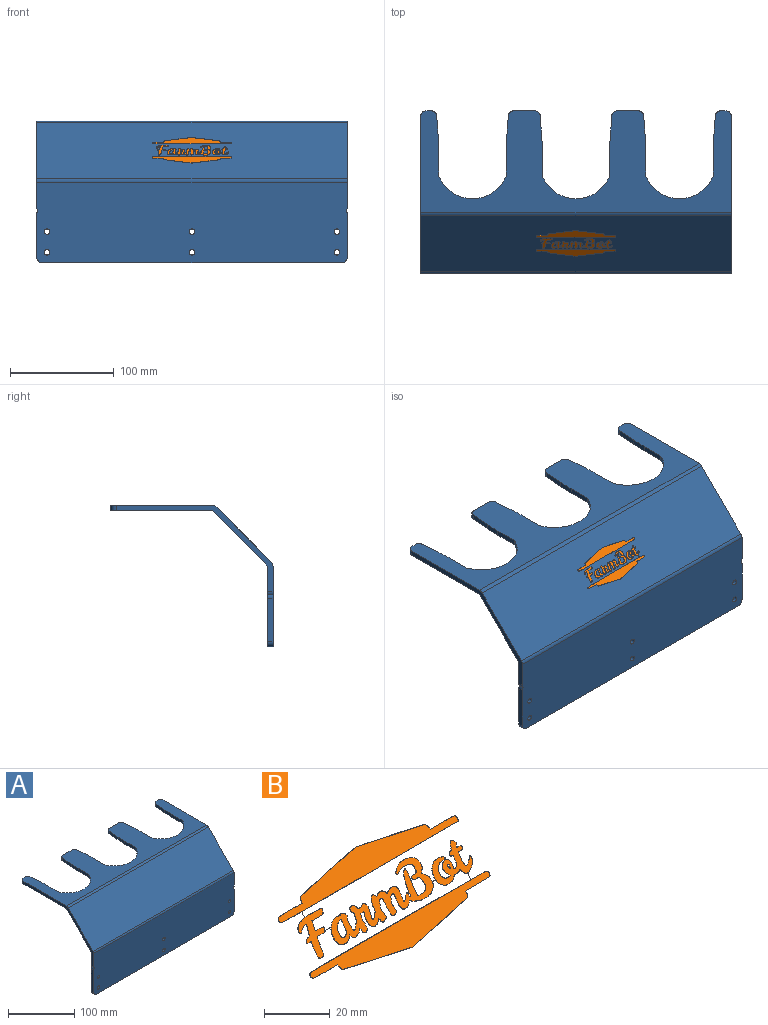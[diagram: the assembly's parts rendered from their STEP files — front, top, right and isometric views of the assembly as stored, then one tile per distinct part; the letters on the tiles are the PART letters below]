
ASSEMBLY  parts=2 mates=1
PART A: 58 faces, bbox 300x156.6x136.6 mm
  f0: plane 300x77.93mm, normal (0,-1,0), area 23234.2mm2, adj f1,f2,f10,f11,f41,f42,f43,f44
  f1: plane 151.57x83.57mm, normal (-1,0,0), area 988.2mm2, adj f0,f3,f4,f6,f39,f40,f42,f45
  f2: plane 151.57x83.57mm, normal (1,0,0), area 988.2mm2, adj f0,f3,f4,f6,f39,f40,f42,f46
  f3: plane 300x77.93mm, normal (0,1,0), area 23234.2mm2, adj f1,f2,f10,f11,f39,f41,f43,f44
  f4: plane 300x97.93mm, normal (0,0,-1), area 13697.5mm2, adj f1,f2,f5,f7,f8,f9,f12,f13
  f5: plane 5.36x5mm, normal (0,1,0), area 26.8mm2, adj f4,f6,f37,f46
  f6: plane 300x97.93mm, normal (0,0,1), area 13697.5mm2, adj f1,f2,f5,f7,f8,f9,f12,f13
  f7: plane 20.73x5mm, normal (0,1,0), area 103.6mm2, adj f4,f6,f28,f38
  f8: plane 20.73x5mm, normal (0,1,0), area 103.6mm2, adj f4,f6,f19,f29
  f9: plane 5.36x5mm, normal (0,1,0), area 26.8mm2, adj f4,f6,f20,f45
  f10: plane 42x5mm, normal (-1,0,0), area 210mm2, adj f0,f3,f43,f55
  f11: plane 42x5mm, normal (1,0,0), area 210mm2, adj f0,f3,f44,f56
  f12: plane 20.82x5mm, normal (-1,0.08,0), area 104.4mm2, adj f4,f6,f18,f19
  f13: plane 20.82x5mm, normal (1,0.08,0), area 104.4mm2, adj f4,f6,f17,f20
  f14: plane 22.43x5mm, normal (1,0,0), area 112.2mm2, adj f4,f6,f15,f17
  f15: cylinder r=35mm len=65mm, axis (0,0,1), area 416.7mm2, adj f4,f6,f14,f16
  f16: plane 22.43x5mm, normal (-1,0,0), area 112.2mm2, adj f4,f6,f15,f18
  f17: cylinder r=200mm len=15.11mm, axis (0,0,1), area 75.6mm2, adj f4,f6,f13,f14
  f18: cylinder r=200mm len=15.11mm, axis (0,0,1), area 75.6mm2, adj f4,f6,f12,f16
  f19: cylinder r=5mm len=5mm, axis (0,0,1), area 37.4mm2, adj f4,f6,f8,f12
  f20: cylinder r=5mm len=5mm, axis (0,0,-1), area 37.4mm2, adj f4,f6,f9,f13
  f21: plane 20.82x5mm, normal (-1,0.08,0), area 104.4mm2, adj f4,f6,f27,f28
  f22: plane 20.82x5mm, normal (1,0.08,0), area 104.4mm2, adj f4,f6,f26,f29
  f23: plane 22.43x5mm, normal (1,0,0), area 112.2mm2, adj f4,f6,f24,f26
  f24: cylinder r=35mm len=65mm, axis (0,0,1), area 416.7mm2, adj f4,f6,f23,f25
  f25: plane 22.43x5mm, normal (-1,0,0), area 112.2mm2, adj f4,f6,f24,f27
  f26: cylinder r=200mm len=15.11mm, axis (0,0,1), area 75.6mm2, adj f4,f6,f22,f23
  f27: cylinder r=200mm len=15.11mm, axis (0,0,1), area 75.6mm2, adj f4,f6,f21,f25
  f28: cylinder r=5mm len=5mm, axis (0,0,1), area 37.4mm2, adj f4,f6,f7,f21
  f29: cylinder r=5mm len=5mm, axis (0,0,-1), area 37.4mm2, adj f4,f6,f8,f22
  f30: plane 20.82x5mm, normal (-1,0.08,0), area 104.4mm2, adj f4,f6,f36,f37
  f31: plane 20.82x5mm, normal (1,0.08,0), area 104.4mm2, adj f4,f6,f35,f38
  f32: plane 22.43x5mm, normal (1,0,0), area 112.2mm2, adj f4,f6,f33,f35
  f33: cylinder r=35mm len=65mm, axis (0,0,1), area 416.7mm2, adj f4,f6,f32,f34
  f34: plane 22.43x5mm, normal (-1,0,0), area 112.2mm2, adj f4,f6,f33,f36
  f35: cylinder r=200mm len=15.11mm, axis (0,0,1), area 75.6mm2, adj f4,f6,f31,f32
  f36: cylinder r=200mm len=15.11mm, axis (0,0,1), area 75.6mm2, adj f4,f6,f30,f34
  f37: cylinder r=5mm len=5mm, axis (0,0,1), area 37.4mm2, adj f4,f5,f6,f30
  f38: cylinder r=5mm len=5mm, axis (0,0,-1), area 37.4mm2, adj f4,f6,f7,f31
  f39: plane 300x53.64mm, normal (0,0.71,-0.71), area 22757.4mm2, adj f1,f2,f3,f4
  f40: plane 300x53.64mm, normal (0,-0.71,0.71), area 22757.4mm2, adj f1,f2,f42,f47
  f41: plane 290x5mm, normal (0,0,-1), area 1450mm2, adj f0,f3,f43,f44
  f42: cylinder r=5mm len=300mm, axis (1,0,0), area 1178.1mm2, adj f0,f1,f2,f40
  f43: cylinder r=5mm len=5mm, axis (0,1,0), area 39.3mm2, adj f0,f3,f10,f41
  f44: cylinder r=5mm len=5mm, axis (0,-1,0), area 39.3mm2, adj f0,f3,f11,f41
  f45: cylinder r=5mm len=5mm, axis (0,0,-1), area 39.3mm2, adj f1,f4,f6,f9
  f46: cylinder r=5mm len=5mm, axis (0,0,1), area 39.3mm2, adj f2,f4,f5,f6
  f47: cylinder r=5mm len=300mm, axis (1,0,0), area 1178.1mm2, adj f1,f2,f6,f40
  f48: cylinder r=2.62mm len=5.25mm, axis (0,-1,0), area 82.5mm2, adj f0,f3
  f49: cylinder r=2.62mm len=5.25mm, axis (0,-1,0), area 82.5mm2, adj f0,f3
  f50: cylinder r=2.62mm len=5.25mm, axis (0,-1,0), area 82.5mm2, adj f0,f3
  f51: cylinder r=2.62mm len=5.25mm, axis (0,-1,0), area 82.5mm2, adj f0,f3
  f52: cylinder r=2.62mm len=5.25mm, axis (0,-1,0), area 82.5mm2, adj f0,f3
  f53: cylinder r=2.62mm len=5.25mm, axis (0,-1,0), area 82.5mm2, adj f0,f3
  f54: cylinder r=5mm len=5mm, axis (0,1,0), area 16.1mm2, adj f0,f1,f3,f55
  f55: cylinder r=5mm len=5mm, axis (0,-1,0), area 16.1mm2, adj f0,f3,f10,f54
  f56: cylinder r=5mm len=5mm, axis (0,1,0), area 16.1mm2, adj f0,f3,f11,f57
  f57: cylinder r=5mm len=5mm, axis (0,-1,0), area 16.1mm2, adj f0,f2,f3,f56
PART B: 232 faces, bbox 77x24.9x24.9 mm
  f0: extruded ~0.63x0.63mm, area 0.1mm2, adj f1,f229,f230,f231
  f1: extruded ~0.72x0.72mm, area 0.1mm2, adj f0,f2,f230,f231
  f2: extruded ~0.56x0.56mm, area 0.1mm2, adj f1,f229,f230,f231
  f3: extruded ~1.22x0.3mm, area 0.1mm2, adj f4,f227,f230,f231
  f4: extruded ~0.97x0.97mm, area 0.1mm2, adj f3,f5,f230,f231
  f5: extruded ~2.07x2.07mm, area 0.3mm2, adj f4,f6,f230,f231
  f6: extruded ~1.87x0.7mm, area 0.2mm2, adj f5,f7,f230,f231
  f7: extruded ~0.65x0.65mm, area 0.1mm2, adj f6,f8,f230,f231
  f8: extruded ~1.21x1.21mm, area 0.2mm2, adj f7,f227,f230,f231
  f9: extruded ~6.37x0.14mm, area 0.6mm2, adj f10,f228,f230,f231
  f10: plane 1.72x1.72mm, normal (1,0,0), area 0.2mm2, adj f9,f11,f230,f231
  f11: extruded ~4.13x2.15mm, area 0.5mm2, adj f10,f12,f230,f231
  f12: extruded ~0.88x0.88mm, area 0.1mm2, adj f11,f13,f230,f231
  f13: extruded ~0.93x0.6mm, area 0.1mm2, adj f12,f14,f230,f231
  f14: extruded ~2.2x1mm, area 0.3mm2, adj f13,f15,f230,f231
  f15: extruded ~2.1x2.1mm, area 0.3mm2, adj f14,f16,f230,f231
  f16: extruded ~1.29x1.29mm, area 0.2mm2, adj f15,f17,f230,f231
  f17: extruded ~1.02x0.2mm, area 0.1mm2, adj f16,f18,f230,f231
  f18: extruded ~1.09x0.36mm, area 0.1mm2, adj f17,f19,f230,f231
  f19: extruded ~0.58x0.58mm, area 0.1mm2, adj f18,f20,f230,f231
  f20: extruded ~0.91x0.29mm, area 0.1mm2, adj f19,f21,f230,f231
  f21: extruded ~0.91x0.14mm, area 0.1mm2, adj f20,f22,f230,f231
  f22: extruded ~0.54x0.54mm, area 0.1mm2, adj f21,f23,f230,f231
  f23: plane 0.47x0.47mm, normal (0.87,-0.35,-0.35), area 0.1mm2, adj f22,f24,f230,f231
  f24: plane 0.48x0.48mm, normal (0.91,0.29,0.29), area 0.1mm2, adj f23,f25,f230,f231
  f25: extruded ~2.37x1.45mm, area 0.4mm2, adj f24,f26,f230,f231
  f26: extruded ~0.75x0.6mm, area 0.1mm2, adj f25,f27,f230,f231
  f27: extruded ~0.87x0.75mm, area 0.1mm2, adj f26,f28,f230,f231
  f28: extruded ~0.41x0.4mm, area 0.1mm2, adj f27,f29,f230,f231
  f29: extruded ~0.51x0.12mm, area 0.1mm2, adj f28,f30,f230,f231
  f30: extruded ~0.74x0.74mm, area 0.1mm2, adj f29,f31,f230,f231
  f31: extruded ~1.02x1.02mm, area 0.1mm2, adj f30,f32,f230,f231
  f32: extruded ~1.01x0.93mm, area 0.2mm2, adj f31,f33,f230,f231
  f33: extruded ~0.78x0.28mm, area 0.1mm2, adj f32,f34,f230,f231
  f34: extruded ~0.97x0.97mm, area 0.1mm2, adj f33,f35,f230,f231
  f35: extruded ~1.06x1.06mm, area 0.1mm2, adj f34,f36,f230,f231
  f36: extruded ~1.45x0.55mm, area 0.2mm2, adj f35,f37,f230,f231
  f37: extruded ~3.02x3.02mm, area 0.6mm2, adj f36,f38,f230,f231
  f38: plane 0.45x0.42mm, normal (-0.74,-0.47,-0.47), area 0.1mm2, adj f37,f39,f230,f231
  f39: plane 0.5x0.17mm, normal (-0.27,0.68,0.68), area 0.1mm2, adj f38,f40,f230,f231
  f40: extruded ~2.56x1.49mm, area 0.4mm2, adj f39,f41,f230,f231
  f41: extruded ~2.21x2.21mm, area 0.4mm2, adj f40,f42,f230,f231
  f42: extruded ~1.46x0.26mm, area 0.1mm2, adj f41,f43,f230,f231
  f43: extruded ~1.25x0.42mm, area 0.2mm2, adj f42,f44,f230,f231
  f44: extruded ~3.53x0.65mm, area 0.4mm2, adj f43,f45,f230,f231
  f45: extruded ~3.22x1.99mm, area 0.4mm2, adj f44,f46,f230,f231
  f46: extruded ~1.84x1.84mm, area 0.3mm2, adj f45,f47,f230,f231
  f47: plane 1.41x0.07mm, normal (0,0.71,0.71), area 0.1mm2, adj f46,f48,f230,f231
  f48: extruded ~1.6x1.6mm, area 0.2mm2, adj f47,f49,f230,f231
  f49: extruded ~1.57x1.22mm, area 0.2mm2, adj f48,f50,f230,f231
  f50: extruded ~0.6x0.55mm, area 0.1mm2, adj f49,f51,f230,f231
  f51: extruded ~2.23x2.23mm, area 0.3mm2, adj f50,f52,f230,f231
  f52: extruded ~2.13x1.57mm, area 0.3mm2, adj f51,f53,f230,f231
  f53: extruded ~4.3x0.34mm, area 0.4mm2, adj f52,f54,f230,f231
  f54: extruded ~3.31x1.78mm, area 0.4mm2, adj f53,f55,f230,f231
  f55: extruded ~1.5x0.37mm, area 0.2mm2, adj f54,f56,f230,f231
  f56: extruded ~3.3x0.58mm, area 0.3mm2, adj f55,f57,f230,f231
  f57: extruded ~2.29x1.48mm, area 0.3mm2, adj f56,f58,f230,f231
  f58: extruded ~0.9x0.9mm, area 0.1mm2, adj f57,f59,f230,f231
  f59: extruded ~1.22x0.4mm, area 0.1mm2, adj f58,f60,f230,f231
  f60: extruded ~1.26x0.32mm, area 0.1mm2, adj f59,f61,f230,f231
  f61: extruded ~0.46x0.46mm, area 0.1mm2, adj f60,f62,f230,f231
  f62: extruded ~1.49x0.53mm, area 0.2mm2, adj f61,f63,f230,f231
  f63: extruded ~1.17x0.41mm, area 0.1mm2, adj f62,f64,f230,f231
  f64: extruded ~2.13x2.13mm, area 0.3mm2, adj f63,f65,f230,f231
  f65: extruded ~2.6x1.08mm, area 0.3mm2, adj f64,f66,f230,f231
  f66: extruded ~1.62x0.27mm, area 0.2mm2, adj f65,f67,f230,f231
  f67: extruded ~3.46x3.46mm, area 0.5mm2, adj f66,f68,f230,f231
  f68: extruded ~2.97x2.97mm, area 0.5mm2, adj f67,f69,f230,f231
  f69: extruded ~4.75x4.75mm, area 0.7mm2, adj f68,f70,f230,f231
  f70: extruded ~0.83x0.83mm, area 0.1mm2, adj f69,f71,f230,f231
  f71: extruded ~0.61x0.61mm, area 0.1mm2, adj f70,f72,f230,f231
  f72: extruded ~0.68x0.68mm, area 0.1mm2, adj f71,f73,f230,f231
  f73: extruded ~1.24x0.75mm, area 0.2mm2, adj f72,f74,f230,f231
  f74: extruded ~1.5x0.81mm, area 0.2mm2, adj f73,f75,f230,f231
  f75: extruded ~1.15x1.15mm, area 0.2mm2, adj f74,f76,f230,f231
  f76: extruded ~2.26x2.26mm, area 0.3mm2, adj f75,f77,f230,f231
  f77: extruded ~0.6x0.51mm, area 0.1mm2, adj f76,f78,f230,f231
  f78: extruded ~3.28x0.68mm, area 0.4mm2, adj f77,f79,f230,f231
  f79: plane 0.34x0.3mm, normal (-0.69,0.51,0.51), area 0mm2, adj f78,f80,f230,f231
  f80: plane 0.32x0.32mm, normal (0.97,0.17,0.17), area 0mm2, adj f79,f81,f230,f231
  f81: extruded ~1.07x0.95mm, area 0.2mm2, adj f80,f82,f230,f231
  f82: extruded ~2.28x0.43mm, area 0.2mm2, adj f81,f83,f230,f231
  f83: extruded ~0.61x0.28mm, area 0.1mm2, adj f82,f84,f230,f231
  f84: extruded ~0.5x0.5mm, area 0.1mm2, adj f83,f85,f230,f231
  f85: extruded ~0.79x0.37mm, area 0.1mm2, adj f84,f86,f230,f231
  f86: extruded ~0.81x0.59mm, area 0.1mm2, adj f85,f87,f230,f231
  f87: extruded ~2.36x2.36mm, area 0.3mm2, adj f86,f88,f230,f231
  f88: plane 0.66x0.66mm, normal (-1,0.07,0.07), area 0.1mm2, adj f87,f89,f230,f231
  f89: plane 0.97x0.71mm, normal (-0.68,0.52,0.52), area 0.1mm2, adj f88,f90,f230,f231
  f90: extruded ~1.73x1.73mm, area 0.4mm2, adj f89,f91,f230,f231
  f91: plane 1.46x1.46mm, normal (0.96,-0.19,-0.19), area 0.2mm2, adj f90,f92,f230,f231
  f92: plane 0.5x0.5mm, normal (0.89,0.32,0.32), area 0.1mm2, adj f91,f93,f230,f231
  f93: extruded ~1.57x0.6mm, area 0.2mm2, adj f92,f94,f230,f231
  f94: extruded ~1.25x0.31mm, area 0.1mm2, adj f93,f95,f230,f231
  f95: extruded ~0.64x0.46mm, area 0.1mm2, adj f94,f96,f230,f231
  f96: extruded ~1.51x0.97mm, area 0.2mm2, adj f95,f97,f230,f231
  f97: extruded ~1.19x0.66mm, area 0.2mm2, adj f96,f98,f230,f231
  f98: extruded ~1x1mm, area 0.1mm2, adj f97,f99,f230,f231
  f99: extruded ~0.88x0.88mm, area 0.1mm2, adj f98,f100,f230,f231
  f100: extruded ~0.9x0.9mm, area 0.1mm2, adj f99,f101,f230,f231
  f101: extruded ~2.35x1.75mm, area 0.3mm2, adj f100,f102,f230,f231
  f102: extruded ~1.36x1.36mm, area 0.2mm2, adj f101,f103,f230,f231
  f103: extruded ~1.75x1.75mm, area 0.2mm2, adj f102,f104,f230,f231
  f104: plane 0.67x0.67mm, normal (0.9,-0.31,-0.31), area 0.1mm2, adj f103,f105,f230,f231
  f105: plane 0.39x0.39mm, normal (0.88,0.34,0.34), area 0.1mm2, adj f104,f106,f230,f231
  f106: extruded ~1.9x0.74mm, area 0.2mm2, adj f105,f107,f230,f231
  f107: extruded ~0.83x0.17mm, area 0.1mm2, adj f106,f108,f230,f231
  f108: extruded ~3.74x0.93mm, area 0.4mm2, adj f107,f109,f230,f231
  f109: extruded ~0.68x0.59mm, area 0.1mm2, adj f108,f110,f230,f231
  f110: plane 2.66x0.07mm, normal (0,0.71,0.71), area 0.3mm2, adj f109,f111,f230,f231
  f111: extruded ~0.91x0.91mm, area 0.1mm2, adj f110,f112,f230,f231
  f112: extruded ~1.71x0.2mm, area 0.2mm2, adj f111,f113,f230,f231
  f113: extruded ~1.58x0.23mm, area 0.2mm2, adj f112,f114,f230,f231
  f114: extruded ~1.2x1.2mm, area 0.2mm2, adj f113,f115,f230,f231
  f115: plane 1.06x1.06mm, normal (0.97,-0.17,-0.17), area 0.1mm2, adj f114,f116,f230,f231
  f116: plane 2.3x0.07mm, normal (0,-0.71,-0.71), area 0.2mm2, adj f115,f117,f230,f231
  f117: extruded ~3.04x0.78mm, area 0.4mm2, adj f116,f118,f230,f231
  f118: extruded ~3.07x0.77mm, area 0.4mm2, adj f117,f119,f230,f231
  f119: extruded ~4.14x0.13mm, area 0.4mm2, adj f118,f120,f230,f231
  f120: plane 1.5x1.5mm, normal (1,0,0), area 0.2mm2, adj f119,f121,f230,f231
  f121: extruded ~29.52x0.08mm, area 3mm2, adj f120,f122,f230,f231
  f122: plane 37.73x0.09mm, normal (0,-0.71,-0.71), area 3.8mm2, adj f121,f123,f230,f231
  f123: plane 0.29x0.29mm, normal (0.78,-0.44,-0.44), area 0mm2, adj f122,f124,f230,f231
  f124: extruded ~1x1mm, area 0.1mm2, adj f123,f125,f230,f231
  f125: extruded ~5.86x0.44mm, area 0.6mm2, adj f124,f126,f230,f231
  f126: plane 4.91x0.07mm, normal (0,0.71,0.71), area 0.5mm2, adj f125,f127,f230,f231
  f127: plane 0.53x0.53mm, normal (0.99,0.09,0.09), area 0.1mm2, adj f126,f128,f230,f231
  f128: extruded ~1.23x1.18mm, area 0.2mm2, adj f127,f129,f230,f231
  f129: extruded ~26.13x3.2mm, area 2.7mm2, adj f128,f130,f230,f231
  f130: extruded ~26.71x3.33mm, area 2.7mm2, adj f129,f131,f230,f231
  f131: extruded ~1.23x1.23mm, area 0.2mm2, adj f130,f132,f230,f231
  f132: plane 0.35x0.35mm, normal (-1,0,0), area 0mm2, adj f131,f133,f230,f231
  f133: plane 4.98x0.07mm, normal (0,0.71,0.71), area 0.5mm2, adj f132,f134,f230,f231
  f134: extruded ~5.43x0.23mm, area 0.5mm2, adj f133,f135,f230,f231
  f135: extruded ~1.36x1.36mm, area 0.2mm2, adj f134,f136,f230,f231
  f136: extruded ~8.52x0.16mm, area 0.9mm2, adj f135,f137,f230,f231
  f137: plane 1.5x1.5mm, normal (-1,0,0), area 0.2mm2, adj f136,f138,f230,f231
  f138: extruded ~1.91x0.32mm, area 0.2mm2, adj f137,f139,f230,f231
  f139: extruded ~2.71x1.78mm, area 0.4mm2, adj f138,f140,f230,f231
  f140: extruded ~1.13x0.65mm, area 0.2mm2, adj f139,f141,f230,f231
  f141: extruded ~2.24x0.85mm, area 0.3mm2, adj f140,f142,f230,f231
  f142: extruded ~0.51x0.21mm, area 0.1mm2, adj f141,f143,f230,f231
  f143: extruded ~1.35x1.35mm, area 0.2mm2, adj f142,f144,f230,f231
  f144: plane 1.17x1.17mm, normal (-0.94,0.24,0.24), area 0.2mm2, adj f143,f145,f230,f231
  f145: plane 0.76x0.28mm, normal (-0.36,0.66,0.66), area 0.1mm2, adj f144,f146,f230,f231
  f146: extruded ~1.49x0.94mm, area 0.2mm2, adj f145,f147,f230,f231
  f147: extruded ~0.92x0.24mm, area 0.1mm2, adj f146,f148,f230,f231
  f148: extruded ~0.86x0.26mm, area 0.1mm2, adj f147,f149,f230,f231
  f149: extruded ~3.92x3.92mm, area 0.6mm2, adj f148,f150,f230,f231
  f150: extruded ~1.96x0.27mm, area 0.2mm2, adj f149,f151,f230,f231
  f151: extruded ~0.85x0.85mm, area 0.1mm2, adj f150,f152,f230,f231
  f152: extruded ~2.71x2.71mm, area 0.4mm2, adj f151,f153,f230,f231
  f153: plane 0.89x0.89mm, normal (0.97,-0.16,-0.16), area 0.1mm2, adj f152,f154,f230,f231
  f154: plane 1.64x0.13mm, normal (-0.05,-0.71,-0.71), area 0.2mm2, adj f153,f155,f230,f231
  f155: extruded ~1.81x0.18mm, area 0.2mm2, adj f154,f156,f230,f231
  f156: extruded ~0.27x0.27mm, area 0mm2, adj f155,f157,f230,f231
  f157: plane 2.66x0.07mm, normal (0,-0.71,-0.71), area 0.3mm2, adj f156,f158,f230,f231
  f158: extruded ~2.39x2.39mm, area 0.4mm2, adj f157,f159,f230,f231
  f159: extruded ~1.69x1.69mm, area 0.2mm2, adj f158,f160,f230,f231
  f160: extruded ~4.82x0.87mm, area 0.5mm2, adj f159,f161,f230,f231
  f161: plane 0.39x0.39mm, normal (0.77,-0.45,-0.45), area 0.1mm2, adj f160,f162,f230,f231
  f162: plane 0.49x0.49mm, normal (-0.93,-0.25,-0.25), area 0.1mm2, adj f161,f163,f230,f231
  f163: extruded ~1.58x0.71mm, area 0.2mm2, adj f162,f164,f230,f231
  f164: extruded ~2.2x0.91mm, area 0.3mm2, adj f163,f165,f230,f231
  f165: plane 0.56x0.43mm, normal (0.68,-0.52,-0.52), area 0.1mm2, adj f164,f166,f230,f231
  f166: plane 0.55x0.55mm, normal (-0.99,-0.09,-0.09), area 0.1mm2, adj f165,f167,f230,f231
  f167: extruded ~0.97x0.97mm, area 0.2mm2, adj f166,f168,f230,f231
  f168: extruded ~1.35x0.52mm, area 0.2mm2, adj f167,f169,f230,f231
  f169: extruded ~1.24x1.24mm, area 0.2mm2, adj f168,f170,f230,f231
  f170: extruded ~1.77x1.77mm, area 0.2mm2, adj f169,f171,f230,f231
  f171: plane 0.76x0.76mm, normal (0.97,-0.17,-0.17), area 0.1mm2, adj f170,f172,f230,f231
  f172: plane 0.75x0.1mm, normal (0.05,-0.71,-0.71), area 0.1mm2, adj f171,f173,f230,f231
  f173: plane 0.75x0.1mm, normal (0.05,-0.71,-0.71), area 0.1mm2, adj f172,f174,f230,f231
  f174: plane 0.35x0.35mm, normal (-0.89,0.32,0.32), area 0mm2, adj f173,f175,f230,f231
  f175: extruded ~2.98x2.98mm, area 0.4mm2, adj f174,f176,f230,f231
  f176: extruded ~1.51x0.79mm, area 0.2mm2, adj f175,f177,f230,f231
  f177: extruded ~2.11x0.76mm, area 0.2mm2, adj f176,f178,f230,f231
  f178: plane 0.54x0.44mm, normal (0.69,-0.51,-0.51), area 0.1mm2, adj f177,f179,f230,f231
  f179: plane 0.52x0.52mm, normal (-0.99,-0.1,-0.1), area 0.1mm2, adj f178,f180,f230,f231
  f180: extruded ~1.78x0.83mm, area 0.3mm2, adj f179,f181,f230,f231
  f181: extruded ~1.22x1.22mm, area 0.2mm2, adj f180,f182,f230,f231
  f182: extruded ~2.13x2.13mm, area 0.3mm2, adj f181,f183,f230,f231
  f183: extruded ~1.53x1.31mm, area 0.2mm2, adj f182,f184,f230,f231
  f184: extruded ~1.54x1.54mm, area 0.2mm2, adj f183,f185,f230,f231
  f185: extruded ~3.02x3.02mm, area 0.4mm2, adj f184,f186,f230,f231
  f186: extruded ~1.82x0.37mm, area 0.2mm2, adj f185,f187,f230,f231
  f187: extruded ~0.71x0.71mm, area 0.1mm2, adj f186,f188,f230,f231
  f188: extruded ~0.92x0.92mm, area 0.1mm2, adj f187,f189,f230,f231
  f189: extruded ~1.87x1.87mm, area 0.3mm2, adj f188,f190,f230,f231
  f190: extruded ~1.33x0.75mm, area 0.2mm2, adj f189,f191,f230,f231
  f191: extruded ~1.63x1.63mm, area 0.2mm2, adj f190,f192,f230,f231
  f192: extruded ~2.62x2.62mm, area 0.5mm2, adj f191,f193,f230,f231
  f193: extruded ~1.85x0.76mm, area 0.2mm2, adj f192,f194,f230,f231
  f194: plane 0.5x0.39mm, normal (0.67,-0.52,-0.52), area 0.1mm2, adj f193,f195,f230,f231
  f195: plane 0.66x0.39mm, normal (-0.56,-0.59,-0.59), area 0.1mm2, adj f194,f196,f230,f231
  f196: extruded ~3.14x0.92mm, area 0.3mm2, adj f195,f197,f230,f231
  f197: extruded ~4.39x0.32mm, area 0.4mm2, adj f196,f198,f230,f231
  f198: extruded ~2.4x1.49mm, area 0.3mm2, adj f197,f199,f230,f231
  f199: extruded ~0.76x0.76mm, area 0.1mm2, adj f198,f200,f230,f231
  f200: plane 1.41x0.07mm, normal (0,-0.71,-0.71), area 0.1mm2, adj f199,f201,f230,f231
  f201: extruded ~0.73x0.73mm, area 0.1mm2, adj f200,f202,f230,f231
  f202: extruded ~2.22x1.53mm, area 0.3mm2, adj f201,f203,f230,f231
  f203: extruded ~1.43x0.13mm, area 0.1mm2, adj f202,f204,f230,f231
  f204: extruded ~2.77x0.81mm, area 0.3mm2, adj f203,f205,f230,f231
  f205: extruded ~1.43x0.37mm, area 0.2mm2, adj f204,f206,f230,f231
  f206: extruded ~1.43x0.27mm, area 0.1mm2, adj f205,f207,f230,f231
  f207: extruded ~0.69x0.43mm, area 0.1mm2, adj f206,f208,f230,f231
  f208: extruded ~1.09x1.03mm, area 0.2mm2, adj f207,f209,f230,f231
  f209: extruded ~0.4x0.11mm, area 0mm2, adj f208,f210,f230,f231
  f210: plane 1.72x1.72mm, normal (-1,0,0), area 0.2mm2, adj f209,f211,f230,f231
  f211: extruded ~31.4x0.1mm, area 3.1mm2, adj f210,f212,f230,f231
  f212: extruded ~37.82x0.23mm, area 3.8mm2, adj f211,f213,f230,f231
  f213: extruded ~0.99x0.99mm, area 0.2mm2, adj f212,f214,f230,f231
  f214: extruded ~5.85x0.56mm, area 0.6mm2, adj f213,f215,f230,f231
  f215: plane 5.03x0.07mm, normal (0,-0.71,-0.71), area 0.5mm2, adj f214,f216,f230,f231
  f216: plane 0.53x0.53mm, normal (-0.99,-0.08,-0.08), area 0.1mm2, adj f215,f217,f230,f231
  f217: extruded ~1.05x1.05mm, area 0.2mm2, adj f216,f218,f230,f231
  f218: extruded ~12.8x1.72mm, area 1.3mm2, adj f217,f219,f230,f231
  f219: extruded ~13.12x1.67mm, area 1.3mm2, adj f218,f220,f230,f231
  f220: extruded ~0.65x0.17mm, area 0.1mm2, adj f219,f221,f230,f231
  f221: extruded ~26.53x3.34mm, area 2.7mm2, adj f220,f222,f230,f231
  f222: extruded ~1.15x1.15mm, area 0.2mm2, adj f221,f223,f230,f231
  f223: plane 0.45x0.45mm, normal (1,-0.03,-0.03), area 0.1mm2, adj f222,f224,f230,f231
  f224: plane 10.5x0.16mm, normal (0.01,-0.71,-0.71), area 1.1mm2, adj f223,f225,f230,f231
  f225: plane 0.29x0.29mm, normal (0.78,-0.44,-0.44), area 0mm2, adj f224,f226,f230,f231
  f226: extruded ~1x1mm, area 0.1mm2, adj f225,f228,f230,f231
  f227: extruded ~2x2mm, area 0.3mm2, adj f3,f8,f230,f231
  f228: extruded ~0.54x0.34mm, area 0.1mm2, adj f9,f226,f230,f231
  f229: extruded ~0.61x0.61mm, area 0.1mm2, adj f0,f2,f230,f231
  f230: plane 77.01x24.78mm, normal (0,-0.71,0.71), area 1191.9mm2, adj f0,f1,f2,f3,f4,f5,f6,f7
  f231: plane 77.01x24.78mm, normal (0,0.71,-0.71), area 1191.9mm2, adj f0,f1,f2,f3,f4,f5,f6,f7
PLACE A t=(0.08,-0.32,-0.32)mm
PLACE B at identity
MATE fastened A.f40 <-> B.f231  axis (0,-0.71,0.71) through (0.08,-78.6,-23.6)mm
